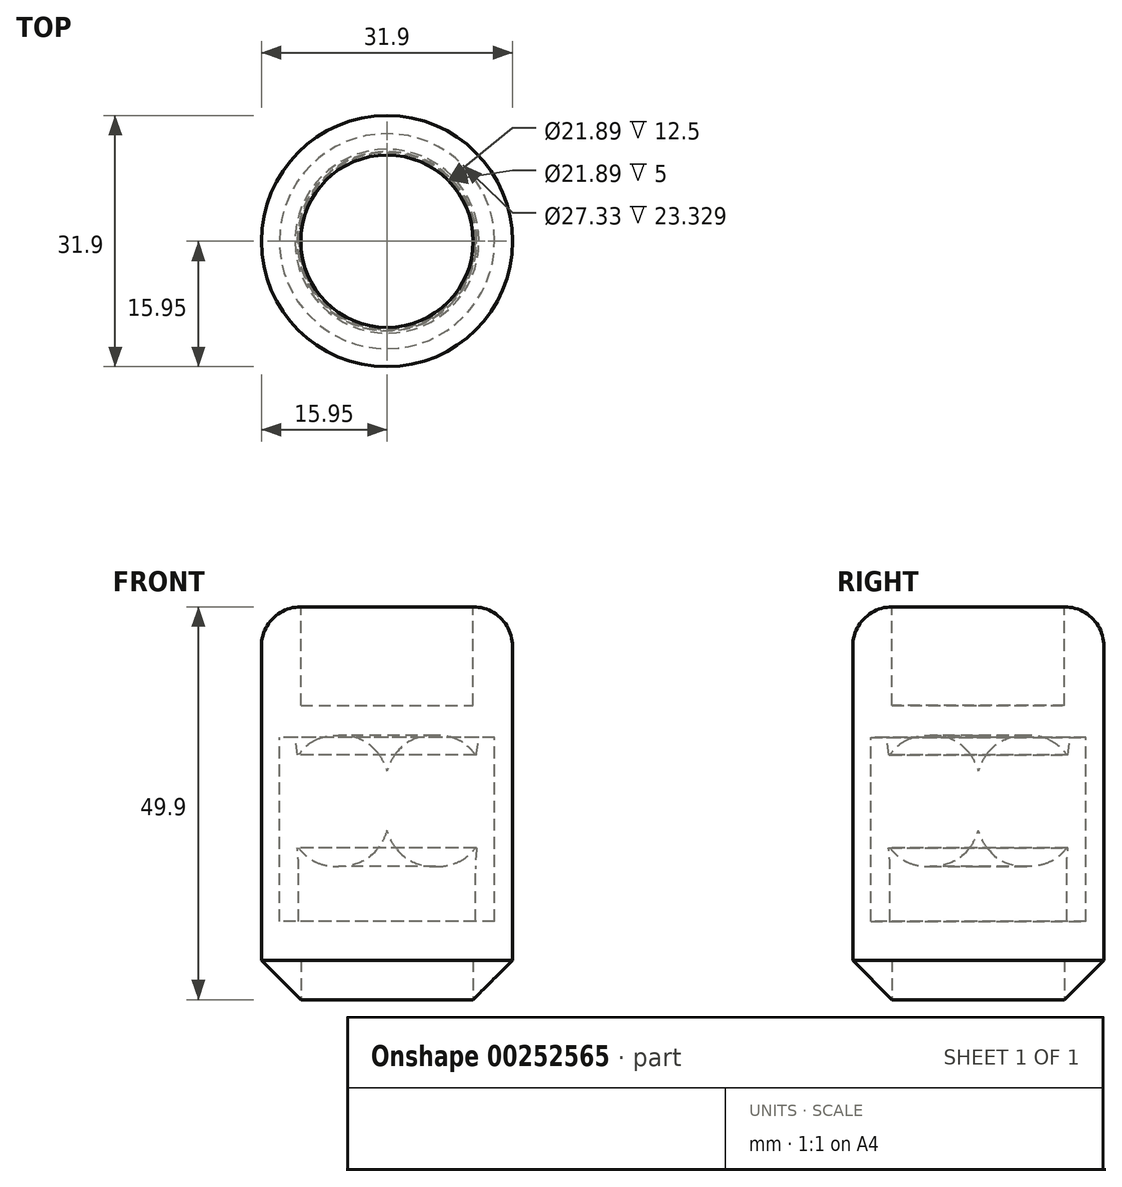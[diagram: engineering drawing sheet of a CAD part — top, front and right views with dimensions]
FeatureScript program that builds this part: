
annotation { "Feature Type Name" : "Feature", "Feature Type Description" : "" }
export const myFeature = defineFeature(function(context is Context, id is Id, definition is map)
    precondition{}
    {
        {
            var Q0;
            Q0=qCreatedBy(makeId("Front.planeOp"),FACE);
            var sketch = newSketch(context, id + "F0", { "sketchPlane" : qUnion([Q0])});
            skLineSegment(sketch, "E0.bottom", {"start": v(-15.95, 21.24) * mm, "end": v(14.05, 21.24) * mm});
            skLineSegment(sketch, "E0.top", {"start": v(-15.95, -28.66) * mm, "end": v(14.05, -28.66) * mm});
            skLineSegment(sketch, "E0.left", {"start": v(-15.95, 21.24) * mm, "end": v(-15.95, -28.66) * mm});
            skLineSegment(sketch, "E0.right", {"start": v(14.05, 21.24) * mm, "end": v(14.05, -28.66) * mm});
            skLineSegment(sketch, "E1", {"start": v(0, 21.24) * mm, "end": v(0, -28.66) * mm});
            skPoint(sketch, "E1.startSnap0", {"position": v(-0.95, 21.24) * mm});
            skText(sketch, "E2", { "text": "Stephen", "fontName": "OpenSans-Regular.ttf"});
            const initialGuessF0  = {"E2": [-0.06026, -0.01146, 1, 0, 0.02166]};
            skSetInitialGuess(sketch, initialGuessF0);
            skSolve(sketch);
        }
        {
            var Q0;
            {var subQ0=sQuery(id+"F0.wireOp",EDGE,"E0.left");Q0=makeQuery(id+"F0.imprint","IMPRINT",FACE,{"disambiguationData":[TD([[makeQuery(id+"F0.imprint","IMPRINT",EDGE,{"derivedFrom":subQ0}),1.0]])]});}
            var Q1;
            Q1=sQuery(id+"F0.wireOp",EDGE,"E1");
            revolve(context, id + "F1", {"entities" : qUnion([Q0]), "axis" : qUnion([Q1]), "revolveType" : RevolveType.FULL});
        }
        {
            var Q0;
            Q0=makeQuery(id+"F1.opRevolve","SWEPT_FACE",FACE,{"disambiguationData":[OSD([sQuery(id+"F0.wireOp",EDGE,"E0.bottom")])]});
            fillet(context, id + "F2", {"entities" : qUnion([Q0]), "radius" : 5 * mm, "tangentPropagation" : true, "allowEdgeOverflow" : false});
        }
        {
            var Q0;
            Q0=makeQuery(id+"F1.opRevolve","SWEPT_FACE",FACE,{"disambiguationData":[OSD([sQuery(id+"F0.wireOp",EDGE,"E0.bottom")])]});
            extrude(context, id + "F3", {"entities" : qUnion([Q0]), "operationType" : NewBodyOperationType.REMOVE, "endBound" : BoundingType.SYMMETRIC, "oppositeDirection" : true, "depth" : 25 * mm});
        }
        {
            var Q0;
            Q0=makeQuery(id+"F1.opRevolve","SWEPT_FACE",FACE,{"disambiguationData":[OSD([sQuery(id+"F0.wireOp",EDGE,"E0.top")])]});
            chamfer(context, id + "F4", {"entities" : qUnion([Q0]), "width" : 5 * mm, "tangentPropagation" : true});
        }
        {
            var Q0;
            Q0=makeQuery(id+"F1.opRevolve","SWEPT_FACE",FACE,{"disambiguationData":[OSD([sQuery(id+"F0.wireOp",EDGE,"E0.top")])]});
            extrude(context, id + "F5", {"entities" : qUnion([Q0]), "operationType" : NewBodyOperationType.REMOVE, "endBound" : BoundingType.SYMMETRIC, "oppositeDirection" : true, "depth" : 10 * mm});
        }
    });
